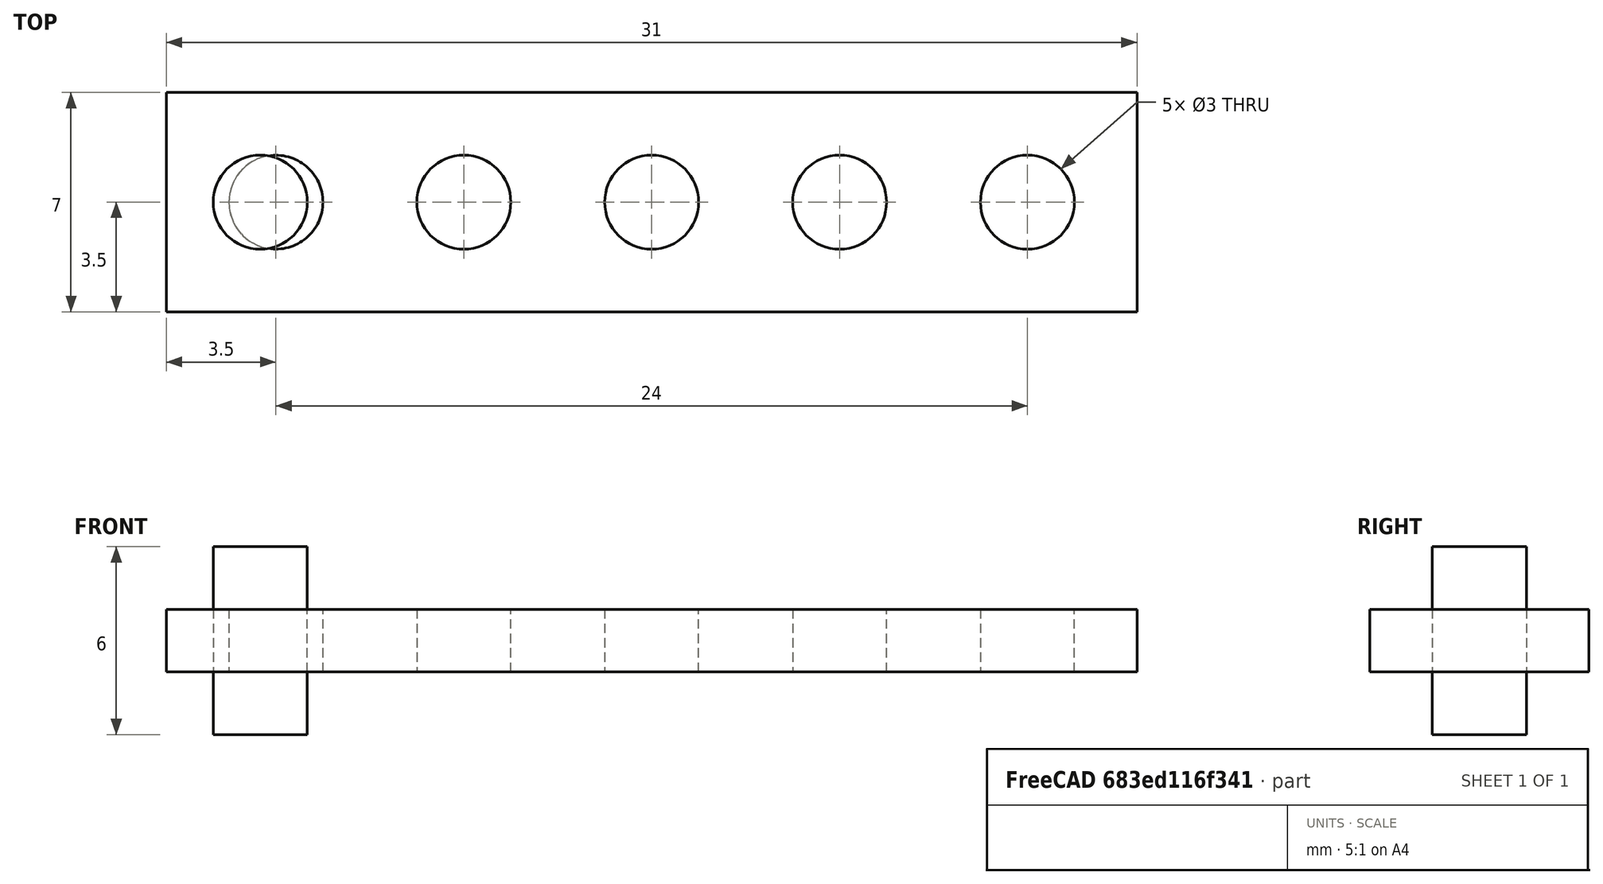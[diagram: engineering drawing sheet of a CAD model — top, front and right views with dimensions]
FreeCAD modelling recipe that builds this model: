
FCSTD DOCUMENT  (FreeCAD 1.0R39285 (Git))
Label: ojt1_t10r01_array_cylinder
License: All rights reserved
objects: Part::Cylinder×1, Part::FeaturePython×1, Part::Box×1, Part::Cut×1
note: 3 computed .brp shape members not serialized (recipe doc carries the construction recipe); baked Part::Feature solids carry a one-line shape summary decoded from their .brp

FEATURE [Part::Cylinder] Cylinder  label="Cilindre"
  Angle = 360
  AttacherType = Attacher::AttachEngine3D
  FirstAngle = 0
  Height = 6
  Placement = pos=(0,0,-2) rot=(0,0,1;0rad)
  Radius = 1.5
  SecondAngle = 0
FEATURE [Part::FeaturePython] Array  # Draft array (typed FeaturePython)
  AlwaysSyncPlacement = false
  Angle = 360
  ArrayType = 0
  Axis = (0,0,1)
  Base = -> Cylinder
  Center = (0,0,0)
  Count = 5
  ExpandArray = false
  Fuse = false
  IntervalAxis = (0,0,0)
  IntervalX = (6,0,0)
  IntervalY = (0,0,0)
  IntervalZ = (0,0,0)
  NumberCircles = 3
  NumberPolar = 5
  NumberX = 5
  NumberY = 1
  NumberZ = 1
  Placement = pos=(0.5,0,0) rot=(0,0,1;0rad)
  PlacementList = 5 placements: arithmetic series from (0,0,-2) step (6,0,0) to (24,0,-2)
  RadialDistance = 50
  ScaleList = (5) [(1,1,1),(1,1,1),(1,1,1),(1,1,1),(1,1,1)]
  Symmetry = 1
  TangentialDistance = 25
FEATURE [Part::Box] Box  label="basis"
  AttacherType = Attacher::AttachEngine3D
  Height = 2
  Length = 31
  Placement = pos=(-3,-3.5,0) rot=(0,-2,1;0rad)
  Width = 7
FEATURE [Part::Cut] Cut  label="array_cylinder"
  Base = -> Box
  Refine = true
  Tool = -> Array
